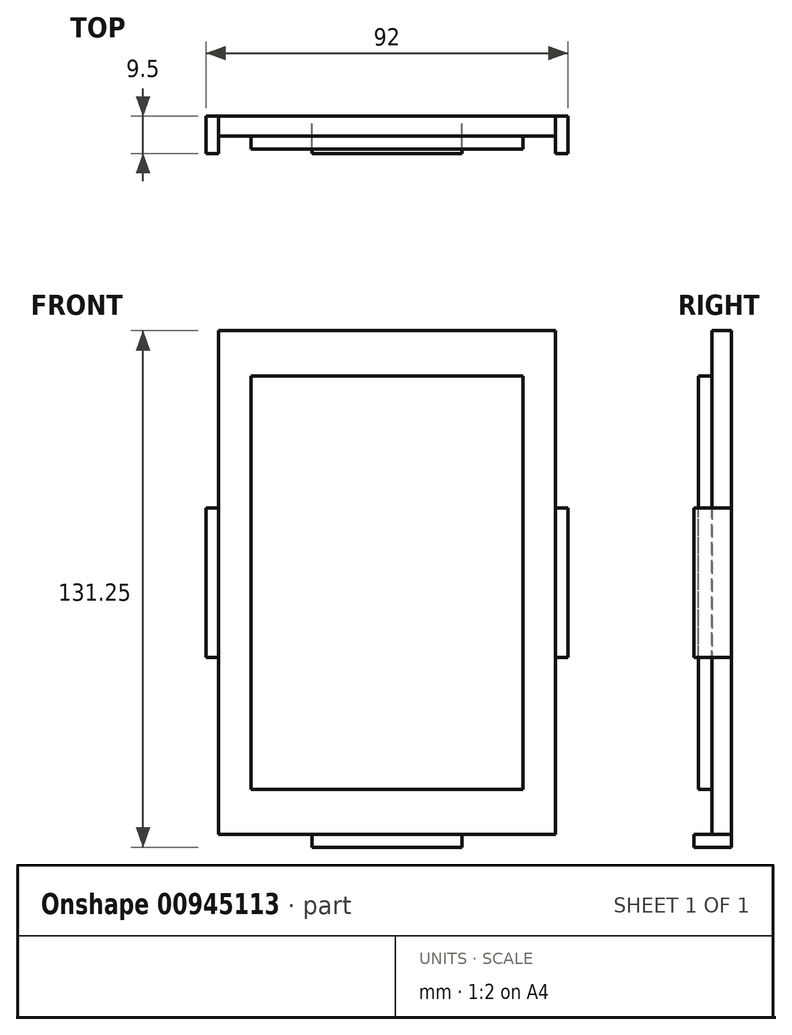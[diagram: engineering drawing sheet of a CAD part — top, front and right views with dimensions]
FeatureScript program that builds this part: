
annotation { "Feature Type Name" : "Feature", "Feature Type Description" : "" }
export const myFeature = defineFeature(function(context is Context, id is Id, definition is map)
    precondition{}
    {
        {
            var Q0;
            Q0=qCreatedBy(makeId("Front.planeOp"),FACE);
            var sketch = newSketch(context, id + "F0", { "sketchPlane" : qUnion([Q0])});
            skLineSegment(sketch, "E0.bottom", {"start": v(-26.91, 112.54) * mm, "end": v(58.59, 112.54) * mm});
            skLineSegment(sketch, "E0.top", {"start": v(-26.91, -15.46) * mm, "end": v(58.59, -15.46) * mm});
            skLineSegment(sketch, "E0.left", {"start": v(-26.91, 112.54) * mm, "end": v(-26.91, -15.46) * mm});
            skLineSegment(sketch, "E0.right", {"start": v(58.59, 112.54) * mm, "end": v(58.59, -15.46) * mm});
            skLineSegment(sketch, "E1", {"start": v(-26.91, 112.54) * mm, "end": v(-26.91, 48.54) * mm});
            skLineSegment(sketch, "E2", {"start": v(-26.91, 48.54) * mm, "end": v(-26.91, -15.46) * mm});
            skLineSegment(sketch, "E3", {"start": v(-26.91, 48.54) * mm, "end": v(58.59, 48.54) * mm});
            skLineSegment(sketch, "E4", {"start": v(58.59, 48.54) * mm, "end": v(58.59, -15.46) * mm});
            skLineSegment(sketch, "E5", {"start": v(-26.91, 48.54) * mm, "end": v(-30.16, 48.54) * mm});
            skLineSegment(sketch, "E6", {"start": v(58.59, 48.54) * mm, "end": v(61.84, 48.54) * mm});
            skLineSegment(sketch, "E7", {"start": v(58.59, 112.54) * mm, "end": v(15.84, 112.54) * mm});
            skLineSegment(sketch, "E8", {"start": v(15.84, 112.54) * mm, "end": v(15.84, -15.46) * mm});
            skLineSegment(sketch, "E9", {"start": v(15.84, -15.46) * mm, "end": v(15.84, -18.7) * mm});
            skLineSegment(sketch, "E10", {"start": v(15.84, 112.54) * mm, "end": v(15.84, 115.8) * mm});
            skLineSegment(sketch, "E11", {"start": v(-30.16, 48.54) * mm, "end": v(-30.16, 29.54) * mm});
            skLineSegment(sketch, "E12", {"start": v(-30.16, 29.54) * mm, "end": v(-30.16, 67.54) * mm});
            skLineSegment(sketch, "E13", {"start": v(-30.16, 67.54) * mm, "end": v(-26.91, 67.54) * mm});
            skLineSegment(sketch, "E14.MirrorCS", {"start": v(61.84, 29.54) * mm, "end": v(61.84, 67.54) * mm});
            skLineSegment(sketch, "E15.MirrorCS", {"start": v(61.84, 67.54) * mm, "end": v(58.59, 67.54) * mm});
            skLineSegment(sketch, "E16", {"start": v(15.84, -18.7) * mm, "end": v(34.84, -18.7) * mm});
            skLineSegment(sketch, "E17", {"start": v(34.84, -18.7) * mm, "end": v(-3.16, -18.7) * mm});
            skLineSegment(sketch, "E18", {"start": v(-3.16, -18.7) * mm, "end": v(-3.16, -15.46) * mm});
            skLineSegment(sketch, "E19", {"start": v(34.84, -18.7) * mm, "end": v(34.84, -15.46) * mm});
            skLineSegment(sketch, "E20.MirrorCS", {"start": v(34.84, 115.8) * mm, "end": v(-3.16, 115.8) * mm});
            skLineSegment(sketch, "E21.MirrorCS", {"start": v(-3.16, 115.8) * mm, "end": v(-3.16, 112.54) * mm});
            skLineSegment(sketch, "E22.MirrorCS", {"start": v(34.84, 115.8) * mm, "end": v(34.84, 112.54) * mm});
            skLineSegment(sketch, "E23", {"start": v(15.84, 48.54) * mm, "end": v(-18.66, 48.54) * mm});
            skLineSegment(sketch, "E24", {"start": v(-18.66, 48.54) * mm, "end": v(50.34, 48.54) * mm});
            skLineSegment(sketch, "E25", {"start": v(50.34, 48.54) * mm, "end": v(50.34, 101.04) * mm});
            skLineSegment(sketch, "E26", {"start": v(50.34, 101.04) * mm, "end": v(50.34, -3.96) * mm});
            skLineSegment(sketch, "E27", {"start": v(50.34, -3.96) * mm, "end": v(15.84, -3.96) * mm});
            skLineSegment(sketch, "E28", {"start": v(50.34, 101.04) * mm, "end": v(15.84, 101.04) * mm});
            skLineSegment(sketch, "E29", {"start": v(-30.16, 29.54) * mm, "end": v(-26.91, 29.54) * mm});
            skLineSegment(sketch, "E30", {"start": v(61.84, 29.54) * mm, "end": v(58.59, 29.54) * mm});
            skLineSegment(sketch, "E31.MirrorCS", {"start": v(-18.66, 101.04) * mm, "end": v(15.84, 101.04) * mm});
            skLineSegment(sketch, "E32.MirrorCS", {"start": v(-18.66, 48.54) * mm, "end": v(-18.66, 101.04) * mm});
            skLineSegment(sketch, "E33.MirrorCS", {"start": v(-18.66, 101.04) * mm, "end": v(-18.66, -3.96) * mm});
            skLineSegment(sketch, "E34.MirrorCS", {"start": v(-18.66, -3.96) * mm, "end": v(15.84, -3.96) * mm});
            skSolve(sketch);
        }
        {
            var Q0;
            {var subQ7=sQuery(id+"F0.wireOp",EDGE,"E31.MirrorCS");Q0=makeQuery(id+"F0.imprint","IMPRINT",FACE,{"disambiguationData":[TD([[makeQuery(id+"F0.imprint","IMPRINT",EDGE,{"derivedFrom":subQ7}),1.0]])]});}
            var Q1;
            {var subQ11=sQuery(id+"F0.wireOp",EDGE,"E28");Q1=makeQuery(id+"F0.imprint","IMPRINT",FACE,{"disambiguationData":[TD([[makeQuery(id+"F0.imprint","IMPRINT",EDGE,{"derivedFrom":subQ11}),-1.0]])]});}
            var Q2;
            {var subQ11=sQuery(id+"F0.wireOp",EDGE,"E27");Q2=makeQuery(id+"F0.imprint","IMPRINT",FACE,{"disambiguationData":[TD([[makeQuery(id+"F0.imprint","IMPRINT",EDGE,{"derivedFrom":subQ11}),1.0]])]});}
            var Q3;
            {var subQ11=sQuery(id+"F0.wireOp",EDGE,"E34.MirrorCS");Q3=makeQuery(id+"F0.imprint","IMPRINT",FACE,{"disambiguationData":[TD([[makeQuery(id+"F0.imprint","IMPRINT",EDGE,{"derivedFrom":subQ11}),-1.0]])]});}
            extrude(context, id + "F1", {"entities" : qUnion([Q0, Q1, Q2, Q3]), "depth" : 5 * mm, "offsetDistance" : 25 * mm});
        }
        {
            var Q0;
            {var subQ0=sQuery(id+"F0.wireOp",EDGE,"E31.MirrorCS");Q0=makeQuery(id+"F0.imprint","IMPRINT",FACE,{"disambiguationData":[TD([[makeQuery(id+"F0.imprint","IMPRINT",EDGE,{"derivedFrom":subQ0}),-1.0]])]});}
            var Q1;
            {var subQ0=sQuery(id+"F0.wireOp",EDGE,"E28");Q1=makeQuery(id+"F0.imprint","IMPRINT",FACE,{"disambiguationData":[TD([[makeQuery(id+"F0.imprint","IMPRINT",EDGE,{"derivedFrom":subQ0}),1.0]])]});}
            var Q2;
            {var subQ0=sQuery(id+"F0.wireOp",EDGE,"E27");Q2=makeQuery(id+"F0.imprint","IMPRINT",FACE,{"disambiguationData":[TD([[makeQuery(id+"F0.imprint","IMPRINT",EDGE,{"derivedFrom":subQ0}),-1.0]])]});}
            var Q3;
            {var subQ0=sQuery(id+"F0.wireOp",EDGE,"E34.MirrorCS");Q3=makeQuery(id+"F0.imprint","IMPRINT",FACE,{"disambiguationData":[TD([[makeQuery(id+"F0.imprint","IMPRINT",EDGE,{"derivedFrom":subQ0}),1.0]])]});}
            extrude(context, id + "F2", {"entities" : qUnion([Q0, Q1, Q2, Q3]), "operationType" : NewBodyOperationType.ADD, "depth" : 8.4 * mm, "offsetDistance" : 25 * mm});
        }
        {
            var Q0;
            {var subQ0=sQuery(id+"F0.wireOp",EDGE,"E5");Q0=makeQuery(id+"F0.imprint","IMPRINT",FACE,{"disambiguationData":[TD([[makeQuery(id+"F0.imprint","IMPRINT",EDGE,{"derivedFrom":subQ0}),-1.0]])]});}
            var Q1;
            {var subQ0=sQuery(id+"F0.wireOp",EDGE,"E5");Q1=makeQuery(id+"F0.imprint","IMPRINT",FACE,{"disambiguationData":[TD([[makeQuery(id+"F0.imprint","IMPRINT",EDGE,{"derivedFrom":subQ0}),1.0]])]});}
            var Q2;
            {var subQ0=sQuery(id+"F0.wireOp",EDGE,"E10");Q2=makeQuery(id+"F0.imprint","IMPRINT",FACE,{"disambiguationData":[TD([[makeQuery(id+"F0.imprint","IMPRINT",EDGE,{"derivedFrom":subQ0}),1.0]])]});}
            var Q3;
            {var subQ0=sQuery(id+"F0.wireOp",EDGE,"E10");Q3=makeQuery(id+"F0.imprint","IMPRINT",FACE,{"disambiguationData":[TD([[makeQuery(id+"F0.imprint","IMPRINT",EDGE,{"derivedFrom":subQ0}),-1.0]])]});}
            var Q4;
            {var subQ0=sQuery(id+"F0.wireOp",EDGE,"E6");Q4=makeQuery(id+"F0.imprint","IMPRINT",FACE,{"disambiguationData":[TD([[makeQuery(id+"F0.imprint","IMPRINT",EDGE,{"derivedFrom":subQ0}),1.0]])]});}
            var Q5;
            {var subQ0=sQuery(id+"F0.wireOp",EDGE,"E6");Q5=makeQuery(id+"F0.imprint","IMPRINT",FACE,{"disambiguationData":[TD([[makeQuery(id+"F0.imprint","IMPRINT",EDGE,{"derivedFrom":subQ0}),-1.0]])]});}
            var Q6;
            {var subQ0=sQuery(id+"F0.wireOp",EDGE,"E9");Q6=makeQuery(id+"F0.imprint","IMPRINT",FACE,{"disambiguationData":[TD([[makeQuery(id+"F0.imprint","IMPRINT",EDGE,{"derivedFrom":subQ0}),1.0]])]});}
            var Q7;
            {var subQ0=sQuery(id+"F0.wireOp",EDGE,"E9");Q7=makeQuery(id+"F0.imprint","IMPRINT",FACE,{"disambiguationData":[TD([[makeQuery(id+"F0.imprint","IMPRINT",EDGE,{"derivedFrom":subQ0}),-1.0]])]});}
            extrude(context, id + "F3", {"entities" : qUnion([Q0, Q1, Q2, Q3, Q4, Q5, Q6, Q7]), "operationType" : NewBodyOperationType.ADD, "depth" : 9.5 * mm, "offsetDistance" : 25 * mm});
        }
    });
